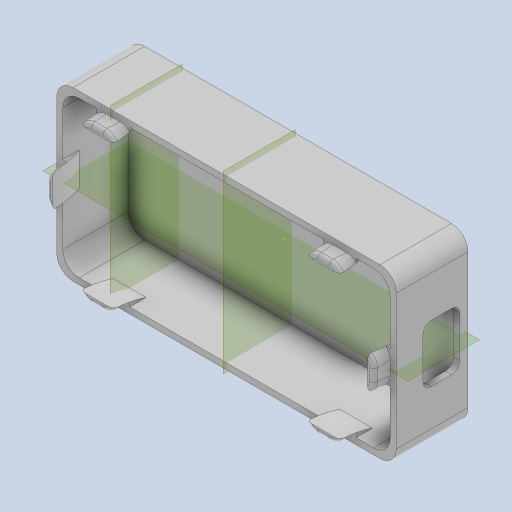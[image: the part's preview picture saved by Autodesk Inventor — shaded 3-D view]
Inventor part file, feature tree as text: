
AUTODESK INVENTOR PART (.ipt)
format: ipt  version: 2024 (Build 280153000, 153)  size: 485,888 bytes
history: native  units: mm
features: fillet x9, sketch x8, extrude x7, other x6, mirror x6, plane x3
ambient origin geometry x8: Origin, YZ Plane, XZ Plane, XY Plane, X Axis, Y Axis, Z Axis, Center Point
bodies: Body1 (feature_tree)
feature tree (39):
  other  "Sólido1"
  extrude  "Extrusión1"  Depth=1.5mm
  extrude  "Extrusión2"  Depth=14.0mm
  extrude  "Extrusión3"  Depth=21.0mm
  fillet  "Empalme1"  Radius=14.0mm
  plane  "Plano de trabajo1"
  plane  "Plano de trabajo2"
  extrude  "Extrusión4"  Depth=2.0mm
  fillet  "Empalme2"  Radius=16.0mm
  mirror  "Simetría1"
  mirror  "Simetría2"
  fillet  "Empalme3"  Radius=2.0mm
  sketch  "Boceto5"  dims[d17=40.0mm d18=19.0mm d24=8.0mm d25=30.0mm]
  extrude  "Extrusión5"  Depth=19.0mm
  fillet  "Empalme4"  Radius=8.0mm
  fillet  "Empalme5"  Radius=30.0mm
  mirror  "Simetría3"
  extrude  "Extrusión6"  Depth=8.0mm TaperAngle=0.0deg
  fillet  "Empalme6"  Radius=2.0mm
  fillet  "Empalme7"  Radius=4.0mm
  mirror  "Simetría4"
  plane  "Plano de trabajo3"
  extrude  "Extrusión7"  Depth=8.0mm
  fillet  "Empalme8"  Radius=30.0mm
  fillet  "Empalme9"  Radius=8.0mm
  mirror  "Simetría5"
  mirror  "Simetría6"
  sketch  "Boceto1"  dims[d4=0.0mm d5=1.5mm]
  sketch  "Boceto2"  dims[d6=16.0mm d7=0.0mm d8=14.0mm]
  sketch  "Boceto3"  dims[d9=9.0mm d10=21.0mm d11=14.0mm]
  sketch  "Boceto4"  dims[d12=13.0mm d13=2.0mm d14=16.0mm d15=0.0mm d16=2.0mm]
  sketch  "Boceto6"  dims[d26=1.5mm d27=8.0mm d28=0.0mm d29=2.0mm d30=4.0mm]
  sketch  "Boceto7"  dims[d31=1.5mm d32=8.0mm d33=30.0mm d34=8.0mm d35=0.0mm]
  sketch  "Boceto8"  dims[d36=3.0mm d37=1.0mm d38=1.5mm d39=8.0mm d40=30.0mm d41=8.0mm d42=0.0mm d43=3.0mm d44=1.0mm d45=27.666667mm d46=1.5mm d47=8.0mm d48=30.0mm d49=1.5mm d50=8.0mm d51=0.0mm d52=3.0mm d53=1.0mm]
  other  "Proyectar aristas de corte1"
  other  "Proyectar aristas de corte2"
  other  "Proyectar aristas de corte3"
  other  "Proyectar aristas de corte4"
  other  "Proyectar aristas de corte5"
